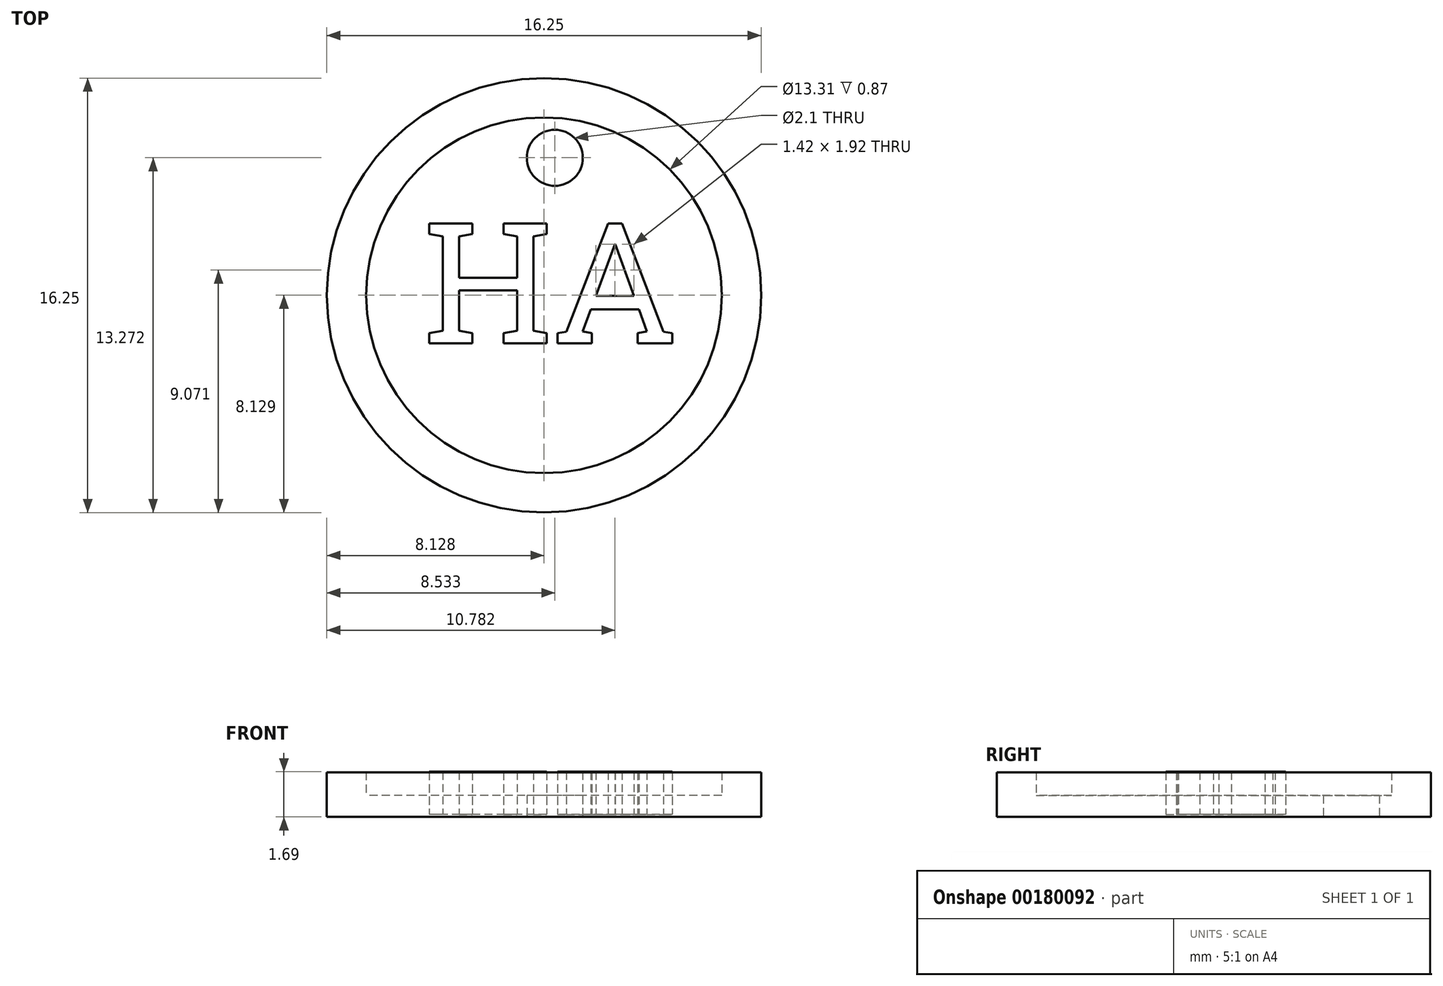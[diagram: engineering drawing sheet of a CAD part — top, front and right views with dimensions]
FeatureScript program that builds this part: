
annotation { "Feature Type Name" : "Feature", "Feature Type Description" : "" }
export const myFeature = defineFeature(function(context is Context, id is Id, definition is map)
    precondition{}
    {
        {
            var Q0;
            Q0=qCreatedBy(makeId("Top.planeOp"),FACE);
            var sketch = newSketch(context, id + "F0", { "sketchPlane" : qUnion([Q0])});
            skCircle(sketch, "E0", {"center": v(-17.25, 12.62) * mm, "radius": 8.12 * mm});
            skCircle(sketch, "E1", {"center": v(-17.25, 12.62) * mm, "radius": 6.65 * mm});
            skText(sketch, "E2", { "text": "HA", "fontName": "RobotoSlab-Regular.ttf"});
            skCircle(sketch, "E3", {"center": v(-16.85, 17.76) * mm, "radius": 1.05 * mm});
            const initialGuessF0  = {"E2": [-0.02766, 0.03004, 1, 0, 0.00454]};
            skSetInitialGuess(sketch, initialGuessF0);
            skSolve(sketch);
        }
        {
            var Q0;
            Q0=makeQuery(id+"F0.imprint","IMPRINT",FACE,{"disambiguationData":[TD([[makeQuery(id+"F0.imprint","IMPRINT",EDGE,{"derivedFrom":sQuery(id+"F0.wireOp",EDGE,"E0")}),1.0]])]});
            extrude(context, id + "F1", {"entities" : qUnion([Q0]), "depth" : 1.67 * mm});
        }
        {
            var Q0;
            Q0=makeQuery(id+"F0.imprint","IMPRINT",FACE,{"disambiguationData":[TD([[makeQuery(id+"F0.imprint","IMPRINT",EDGE,{"derivedFrom":sQuery(id+"F0.wireOp",EDGE,"E1")}),1.0]])]});
            extrude(context, id + "F2", {"entities" : qUnion([Q0]), "operationType" : NewBodyOperationType.ADD, "depth" : .8 * mm});
        }
        {
            var Q0;
            Q0=makeQuery(id+"F0.imprint","IMPRINT",FACE,{"disambiguationData":[TD([[makeQuery(id+"F0.imprint","IMPRINT",EDGE,{"derivedFrom":sQuery(id+"F0.wireOp",EDGE,"E2.sketch_text.stroke-30")}),-1.0]])]});
            var Q1;
            Q1=makeQuery(id+"F0.imprint","IMPRINT",FACE,{"disambiguationData":[TD([[makeQuery(id+"F0.imprint","IMPRINT",EDGE,{"derivedFrom":sQuery(id+"F0.wireOp",EDGE,"E2.sketch_text.stroke-0")}),-1.0]])]});
            extrude(context, id + "F3", {"entities" : qUnion([Q0, Q1]), "depth" : 1.6 * mm});
        }
        {
            var Q0;
            Q0=makeQuery(id+"F3.opExtrude","SWEPT_BODY",BODY,{"disambiguationData":[OSD([sQuery(id+"F0.wireOp",EDGE,"E2.sketch_text.stroke-30"),sQuery(id+"F0.wireOp",EDGE,"E2.sketch_text.stroke-31"),sQuery(id+"F0.wireOp",EDGE,"E2.sketch_text.stroke-32"),sQuery(id+"F0.wireOp",EDGE,"E2.sketch_text.stroke-33"),sQuery(id+"F0.wireOp",EDGE,"E2.sketch_text.stroke-34"),sQuery(id+"F0.wireOp",EDGE,"E2.sketch_text.stroke-35"),sQuery(id+"F0.wireOp",EDGE,"E2.sketch_text.stroke-36"),sQuery(id+"F0.wireOp",EDGE,"E2.sketch_text.stroke-37"),sQuery(id+"F0.wireOp",EDGE,"E2.sketch_text.stroke-38"),sQuery(id+"F0.wireOp",EDGE,"E2.sketch_text.stroke-39"),sQuery(id+"F0.wireOp",EDGE,"E2.sketch_text.stroke-40"),sQuery(id+"F0.wireOp",EDGE,"E2.sketch_text.stroke-41"),sQuery(id+"F0.wireOp",EDGE,"E2.sketch_text.stroke-42"),sQuery(id+"F0.wireOp",EDGE,"E2.sketch_text.stroke-43"),sQuery(id+"F0.wireOp",EDGE,"E2.sketch_text.stroke-44"),sQuery(id+"F0.wireOp",EDGE,"E2.sketch_text.stroke-45"),sQuery(id+"F0.wireOp",EDGE,"E2.sketch_text.stroke-46"),sQuery(id+"F0.wireOp",EDGE,"E2.sketch_text.stroke-47"),sQuery(id+"F0.wireOp",EDGE,"E2.sketch_text.stroke-48"),sQuery(id+"F0.wireOp",EDGE,"E2.sketch_text.stroke-49")])]});
            var Q1;
            Q1=makeQuery(id+"F3.opExtrude","SWEPT_BODY",BODY,{"disambiguationData":[OSD([sQuery(id+"F0.wireOp",EDGE,"E2.sketch_text.stroke-0"),sQuery(id+"F0.wireOp",EDGE,"E2.sketch_text.stroke-1"),sQuery(id+"F0.wireOp",EDGE,"E2.sketch_text.stroke-2"),sQuery(id+"F0.wireOp",EDGE,"E2.sketch_text.stroke-3"),sQuery(id+"F0.wireOp",EDGE,"E2.sketch_text.stroke-4"),sQuery(id+"F0.wireOp",EDGE,"E2.sketch_text.stroke-5"),sQuery(id+"F0.wireOp",EDGE,"E2.sketch_text.stroke-6"),sQuery(id+"F0.wireOp",EDGE,"E2.sketch_text.stroke-7"),sQuery(id+"F0.wireOp",EDGE,"E2.sketch_text.stroke-8"),sQuery(id+"F0.wireOp",EDGE,"E2.sketch_text.stroke-9"),sQuery(id+"F0.wireOp",EDGE,"E2.sketch_text.stroke-10"),sQuery(id+"F0.wireOp",EDGE,"E2.sketch_text.stroke-11"),sQuery(id+"F0.wireOp",EDGE,"E2.sketch_text.stroke-12"),sQuery(id+"F0.wireOp",EDGE,"E2.sketch_text.stroke-13"),sQuery(id+"F0.wireOp",EDGE,"E2.sketch_text.stroke-14"),sQuery(id+"F0.wireOp",EDGE,"E2.sketch_text.stroke-15"),sQuery(id+"F0.wireOp",EDGE,"E2.sketch_text.stroke-16"),sQuery(id+"F0.wireOp",EDGE,"E2.sketch_text.stroke-17"),sQuery(id+"F0.wireOp",EDGE,"E2.sketch_text.stroke-18"),sQuery(id+"F0.wireOp",EDGE,"E2.sketch_text.stroke-19"),sQuery(id+"F0.wireOp",EDGE,"E2.sketch_text.stroke-20"),sQuery(id+"F0.wireOp",EDGE,"E2.sketch_text.stroke-21"),sQuery(id+"F0.wireOp",EDGE,"E2.sketch_text.stroke-22"),sQuery(id+"F0.wireOp",EDGE,"E2.sketch_text.stroke-23"),sQuery(id+"F0.wireOp",EDGE,"E2.sketch_text.stroke-24"),sQuery(id+"F0.wireOp",EDGE,"E2.sketch_text.stroke-25"),sQuery(id+"F0.wireOp",EDGE,"E2.sketch_text.stroke-26"),sQuery(id+"F0.wireOp",EDGE,"E2.sketch_text.stroke-27"),sQuery(id+"F0.wireOp",EDGE,"E2.sketch_text.stroke-28"),sQuery(id+"F0.wireOp",EDGE,"E2.sketch_text.stroke-29")])]});
            transform(context, id + "F4", {"entities" : qUnion([Q0, Q1]), "transformType" : TransformType.TRANSLATION_3D, "dx" : 5.9 * mm, "dy" : -19.22 * mm, "dz" : 0.1 * mm, "makeCopy" : false});
        }
    });
